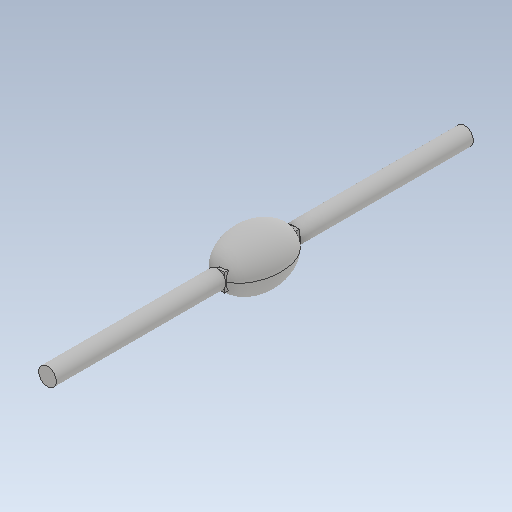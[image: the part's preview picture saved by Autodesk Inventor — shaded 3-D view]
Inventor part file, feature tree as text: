
AUTODESK INVENTOR PART (.ipt)
format: ipt  version: 2020 (Build 240168000, 168)  size: 172,544 bytes
history: native  units: mm
features: sketch x7, extrude x6, plane x2, revolve x1
ambient origin geometry x8: Origin, YZ Plane, XZ Plane, XY Plane, X Axis, Y Axis, Z Axis, Center Point
bodies: Body1 (feature_tree)
feature tree (16):
  revolve  "Revolution2"  Angle=90.0deg
  plane  "Work Plane2"
  extrude  "Extrusion1"  Depth=47.625mm
  plane  "Work Plane3"
  extrude  "Extrusion2"  Depth=100.0mm
  extrude  "Extrusion3"  Depth=46.103mm TaperAngle=0.0deg
  extrude  "Extrusion4"  Depth=7.794mm TaperAngle=0.0deg
  extrude  "Extrusion5"  [1 undecoded]
  extrude  "Extrusion6"  [1 undecoded]
  sketch  "Sketch3"  dims[d6=100.0mm d7=90.0deg]
  sketch  "Sketch4"  dims[d8=-100.0mm d9=47.625mm]
  sketch  "Sketch5"  dims[d10=406.515mm d11=0.0mm d12=100.0mm]
  sketch  "Sketch6"  dims[d13=406.515mm d14=0.0mm d15=46.103mm d16=0.0mm]
  sketch  "Sketch7"  dims[d17=46.103mm d18=0.0mm d19=7.794mm d20=0.0mm]
  sketch  "Sketch8"  dims[d21=20.0mm d22=0.0mm]
  sketch  "Sketch9"
note: 2 required parameter values undecoded (feature->parameter linkage not recoverable at this tier; creation-order binding heuristic only, values carry confidence <= 0.55)
